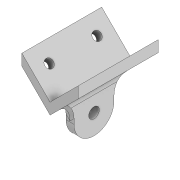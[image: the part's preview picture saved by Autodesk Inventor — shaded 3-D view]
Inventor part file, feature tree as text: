
AUTODESK INVENTOR PART (.ipt)
format: ipt  version: 2022 (Build 260153000, 153)  size: 171,520 bytes
history: native  units: mm
features: extrude x4, sketch x4, projected_geometry x3, plane x2, fillet x2, other x1, mirror x1
ambient origin geometry x8: Origin, YZ Plane, XZ Plane, XY Plane, X Axis, Y Axis, Z Axis, Center Point
bodies: Body1 (feature_tree)
feature tree (17):
  other  "Sólido1"
  extrude  "Extrusión1"  Depth=15.0mm
  plane  "Plano de trabajo1"
  extrude  "Extrusión2"  Depth=3.0mm
  fillet  "Empalme1"  Radius=30.0mm
  fillet  "Empalme2"  Radius=3.0mm
  extrude  "Extrusión3"  Depth=15.0mm
  extrude  "Extrusión4"  Depth=7.5mm
  plane  "Plano de trabajo2"
  mirror  "Simetría1"
  sketch  "Boceto1"  dims[d0=15.0mm d2=15.0mm]
  sketch  "Boceto2"  dims[d6=3.0mm d7=3.0mm d8=30.0mm d9=0.0mm d10=3.0mm]
  projected_geometry  "Contorno proyectado1"
  sketch  "Boceto3"  dims[d11=1.5mm d12=15.0mm]
  projected_geometry  "Contorno proyectado2"
  sketch  "Boceto4"  dims[d13=15.0mm d14=0.0mm d15=7.5mm d16=4.0mm d17=4.0mm d18=0.0mm d19=0.0mm d20=3.2mm d21=3.2mm d22=18.0mm d23=9.0mm d24=3.0mm d25=0.0mm d26=0.0mm]
  projected_geometry  "Contorno proyectado3"
